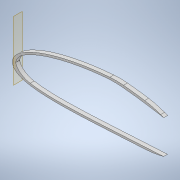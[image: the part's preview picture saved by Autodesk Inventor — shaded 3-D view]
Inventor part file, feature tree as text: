
AUTODESK INVENTOR PART (.ipt)
format: ipt  version: 2022.1 (Build 261234020, 234B)  size: 617,984 bytes
history: native  units: mm
features: sketch x8, extrude x7, projected_geometry x5, thicken_offset x4, fillet x4, shell x1, plane x1, other x1
ambient origin geometry x8: Origin, YZ Plane, XZ Plane, XY Plane, X Axis, Y Axis, Z Axis, Center Point
bodies: Solid1 (feature_tree)
feature tree (31):
  extrude  "Extrusion1"  Depth=3.0mm
  shell  "Shell1"  Thickness=1.0mm
  thicken_offset  "Thicken1"
  extrude  "Extrusion27"  TaperAngle=0.0deg  [1 undecoded]
  thicken_offset  "Thicken3"
  extrude  "Extrusion29"  Depth=20.0mm
  plane  "Work Plane5"
  other  "Bend Part2"
  thicken_offset  "Thicken5"
  extrude  "Extrusion30"  Depth=5.0mm TaperAngle=0.0deg
  fillet  "Fillet6"  Radius=10.0mm
  extrude  "Extrusion31"  Depth=1.0mm
  fillet  "Fillet7"  Radius=50.0mm
  extrude  "Extrusion32"  Depth=5.0mm TaperAngle=0.0deg
  fillet  "Fillet8"  Radius=500.0mm
  thicken_offset  "Thicken6"
  extrude  "Extrusion33"  Depth=60.0mm
  fillet  "Fillet9"  Radius=600.0mm
  sketch  "Sketch3"  dims[d0=5.0mm d1=0.0mm d2=3.0mm d159=1.0mm d160=2.0mm]
  sketch  "Sketch48"  dims[d236=190.0mm d237=0.0mm d238=0.0mm]
  sketch  "Sketch55"  dims[d249=2.0mm d250=1.0mm d254=20.0mm]
  projected_geometry  "Projected Loop32"
  sketch  "Sketch57"  dims[d255=8.0mm d256=5.0mm d257=0.0mm d262=10.0mm d263=0.174533mm]
  sketch  "Sketch58"  dims[d264=1.0mm d265=1.0mm d268=50.0mm]
  projected_geometry  "Projected Loop34"
  sketch  "Sketch59"  dims[d269=9.0mm d270=5.0mm d271=0.0mm d272=500.0mm]
  projected_geometry  "Projected Loop35"
  sketch  "Sketch60"  dims[d273=200.0mm d274=60.0mm d275=600.0mm]
  projected_geometry  "Projected Loop36"
  sketch  "Sketch61"  dims[d276=5.0mm d277=0.0mm d278=100.0mm d279=5.0mm d280=60.0mm d281=500.0mm d282=10.0mm d283=0.0mm d284=100.0mm d285=2.5mm d286=3.0mm d287=10.0mm d288=0.0mm d289=100.0mm]
  projected_geometry  "Projected Loop37"
note: 1 required parameter value undecoded (feature->parameter linkage not recoverable at this tier; creation-order binding heuristic only, values carry confidence <= 0.55)
